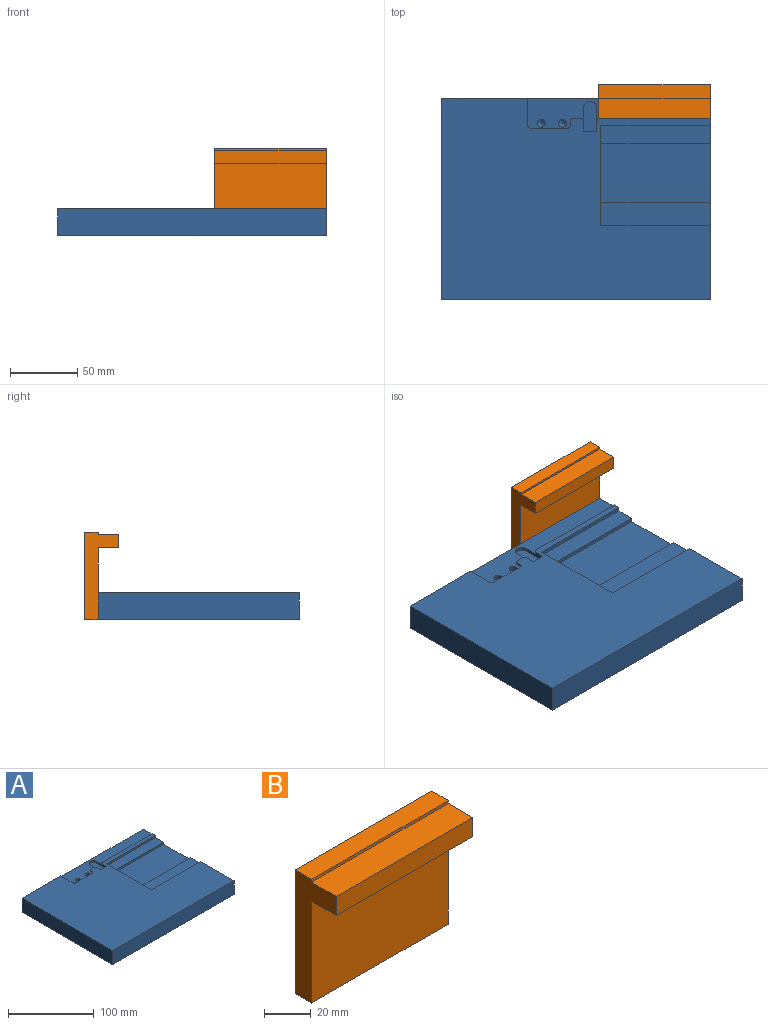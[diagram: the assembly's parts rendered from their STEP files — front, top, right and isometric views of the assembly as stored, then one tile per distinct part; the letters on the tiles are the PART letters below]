
ASSEMBLY  parts=2 mates=1
PART A: 34 faces, bbox 200x150x20 mm
  f0: plane 150x20mm, normal (1,0,0), area 2621.4mm2, adj f1,f2,f3,f5,f6,f7,f27,f28
  f1: plane 136x22.3mm, normal (0,0,1), area 2123.4mm2, adj f0,f3,f7,f8,f9,f10,f11,f12
  f2: plane 200x150mm, normal (0,0,1), area 21538.3mm2, adj f0,f3,f4,f5,f7,f8,f9,f10
  f3: plane 200x20mm, normal (0,1,0), area 3796mm2, adj f0,f1,f2,f4,f6,f8
  f4: plane 150x20mm, normal (-1,0,0), area 3000mm2, adj f2,f3,f5,f6
  f5: plane 200x20mm, normal (0,-1,0), area 4000mm2, adj f0,f2,f4,f6
  f6: plane 200x150mm, normal (0,0,-1), area 30000mm2, adj f0,f3,f4,f5
  f7: plane 82.4x1.5mm, normal (0,1,0), area 123.6mm2, adj f0,f1,f2,f19
  f8: plane 20.3x1.5mm, normal (1,0,0), area 30.5mm2, adj f1,f2,f3,f17
  f9: plane 28x1.5mm, normal (0,1,0), area 42mm2, adj f1,f2,f17,f18
  f10: plane 3.1x1.5mm, normal (-1,0,0), area 4.7mm2, adj f1,f2,f18,f20
  f11: plane 5.6x1.5mm, normal (0,1,0), area 8.4mm2, adj f1,f2,f20,f21
  f12: plane 17x4mm, normal (-1,0,0), area 53.6mm2, adj f1,f2,f14,f15,f16,f19
  f13: plane 17x4mm, normal (1,0,0), area 53.6mm2, adj f1,f2,f14,f15,f16,f21
  f14: plane 10x4mm, normal (0,1,0), area 40mm2, adj f2,f12,f13,f15
  f15: plane 22x10mm, normal (0,0,1), area 209.3mm2, adj f12,f13,f14,f16
  f16: cylinder r=5mm len=10mm, axis (0,0,1), area 39.3mm2, adj f1,f12,f13,f15
  f17: cylinder r=2mm len=2mm, axis (0,0,-1), area 4.7mm2, adj f1,f2,f8,f9
  f18: cylinder r=2mm len=2mm, axis (0,0,1), area 4.7mm2, adj f1,f2,f9,f10
  f19: cylinder r=2mm len=2mm, axis (0,0,-1), area 4.7mm2, adj f1,f2,f7,f12
  f20: cylinder r=2mm len=2mm, axis (0,0,-1), area 4.7mm2, adj f1,f2,f10,f11
  f21: cylinder r=2mm len=2mm, axis (0,0,1), area 4.7mm2, adj f1,f2,f11,f13
  f22: cone r=0mm half-angle=59deg, axis (0,0,1), area 33mm2, adj f23
  f23: cylinder r=3mm len=12mm, axis (0,0,1), area 226.2mm2, adj f1,f22
  f24: cone r=0mm half-angle=59deg, axis (0,0,1), area 33mm2, adj f25
  f25: cylinder r=3mm len=12mm, axis (0,0,1), area 226.2mm2, adj f1,f24
  f26: plane 74.6x6mm, normal (1,0,0), area 355.8mm2, adj f2,f27,f28,f29,f30,f31,f32,f33
  f27: plane 81.4x3mm, normal (0,-1,0), area 244.2mm2, adj f0,f2,f26,f28
  f28: plane 81.4x13.6mm, normal (0,0,1), area 1107mm2, adj f0,f26,f27,f29
  f29: plane 81.4x3mm, normal (0,-1,0), area 244.2mm2, adj f0,f26,f28,f31
  f30: plane 81.4x3mm, normal (0,1,0), area 244.2mm2, adj f0,f26,f31,f33
  f31: plane 81.4x44mm, normal (0,0,1), area 3581.6mm2, adj f0,f26,f29,f30
  f32: plane 81.4x3mm, normal (0,1,0), area 244.2mm2, adj f0,f2,f26,f33
  f33: plane 81.4x17mm, normal (0,0,1), area 1383.8mm2, adj f0,f26,f30,f32
PART B: 10 faces, bbox 83x25x65 mm
  f0: plane 83x1.5mm, normal (0,-1,0), area 124.5mm2, adj f2,f4,f5,f8
  f1: plane 83x53.5mm, normal (0,-1,0), area 4440.5mm2, adj f2,f4,f6,f7
  f2: plane 65x25mm, normal (1,0,0), area 800mm2, adj f0,f1,f3,f5,f6,f7,f8,f9
  f3: plane 83x65mm, normal (0,1,0), area 5395mm2, adj f2,f4,f5,f6
  f4: plane 65x25mm, normal (-1,0,0), area 800mm2, adj f0,f1,f3,f5,f6,f7,f8,f9
  f5: plane 83x10mm, normal (0,0,1), area 830mm2, adj f0,f2,f3,f4
  f6: plane 83x10mm, normal (0,0,-1), area 830mm2, adj f1,f2,f3,f4
  f7: plane 83x15mm, normal (0,0,-1), area 1245mm2, adj f1,f2,f4,f9
  f8: plane 83x15mm, normal (0,0,1), area 1245mm2, adj f0,f2,f4,f9
  f9: plane 83x10mm, normal (0,-1,0), area 830mm2, adj f2,f4,f7,f8
PLACE A t=(29.13,43.6,-3.57)mm
PLACE B t=(87.63,123.6,-3.57)mm
MATE fastened B.f6 <-> A.f6  axis (0,0,1) through (129.13,118.6,-3.57)mm
